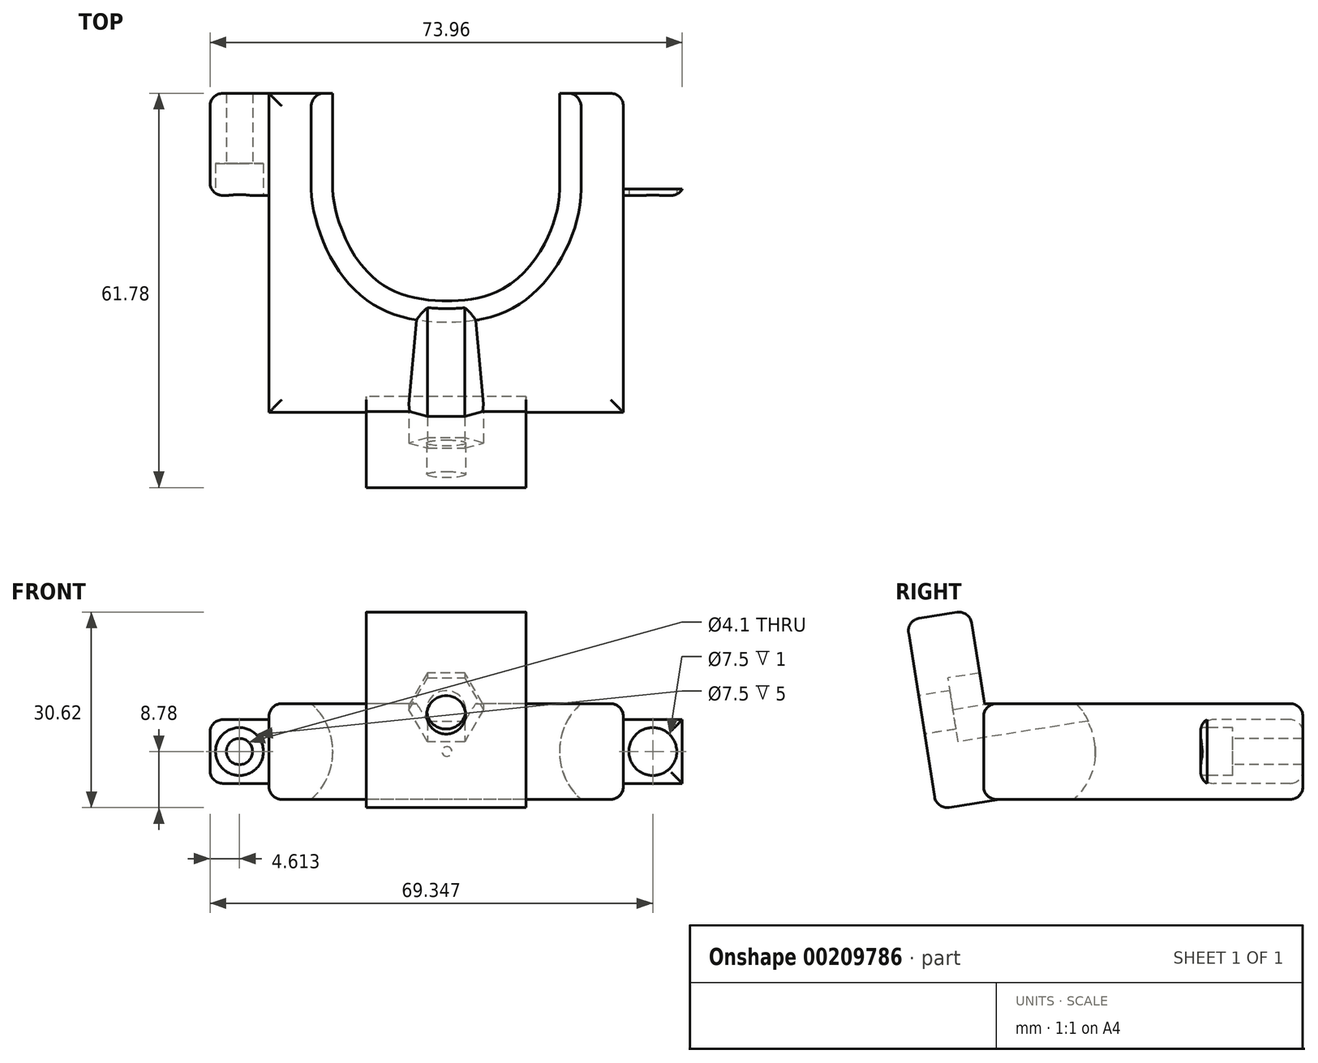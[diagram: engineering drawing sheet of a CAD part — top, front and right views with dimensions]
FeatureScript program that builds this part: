
annotation { "Feature Type Name" : "Feature", "Feature Type Description" : "" }
export const myFeature = defineFeature(function(context is Context, id is Id, definition is map)
    precondition{}
    {
        {
            var Q0;
            Q0=qCreatedBy(makeId("Front.planeOp"),FACE);
            var sketch = newSketch(context, id + "F0", { "sketchPlane" : qUnion([Q0])});
            skCircle(sketch, "E0", {"center": v(-32.37, 0) * mm, "radius": 2.05 * mm});
            skCircle(sketch, "E1.MirrorC", {"center": v(32.37, 0) * mm, "radius": 2.05 * mm});
            skLineSegment(sketch, "E2", {"start": v(-32.37, 0) * mm, "end": v(32.37, 0) * mm, "construction": true});
            skPoint(sketch, "E3", {"position": v(0, 0) * mm});
            skPoint(sketch, "E4", {"position": v(17.75, 0) * mm});
            skPoint(sketch, "E5", {"position": v(-17.75, 0) * mm});
            skLineSegment(sketch, "E6", {"start": v(27.75, -10) * mm, "end": v(27.75, 10) * mm});
            skLineSegment(sketch, "E7", {"start": v(-27.75, -10) * mm, "end": v(-27.75, 10) * mm});
            skPoint(sketch, "E8", {"position": v(-27.75, 0) * mm});
            skPoint(sketch, "E9", {"position": v(27.75, 0) * mm});
            skArc(sketch, "E10", {"start": v(-27.75, -10) * mm, "mid": v(-17.75, 0) * mm, "end": v(-27.75, 10) * mm});
            skArc(sketch, "E11", {"start": v(27.75, 10) * mm, "mid": v(17.75, 0) * mm, "end": v(27.75, -10) * mm});
            skLineSegment(sketch, "E12.bottom", {"start": v(-27.75, -5) * mm, "end": v(-36.98, -5) * mm});
            skLineSegment(sketch, "E12.top", {"start": v(-27.75, 5) * mm, "end": v(-36.98, 5) * mm});
            skLineSegment(sketch, "E12.left", {"start": v(-27.75, -5) * mm, "end": v(-27.75, 5) * mm});
            skLineSegment(sketch, "E12.right", {"start": v(-36.98, -5) * mm, "end": v(-36.98, 5) * mm});
            skLineSegment(sketch, "E13.bottom", {"start": v(27.75, 5) * mm, "end": v(36.98, 5) * mm});
            skLineSegment(sketch, "E13.top", {"start": v(27.75, -5) * mm, "end": v(36.98, -5) * mm});
            skLineSegment(sketch, "E13.left", {"start": v(27.75, 5) * mm, "end": v(27.75, -5) * mm});
            skLineSegment(sketch, "E13.right", {"start": v(36.98, 5) * mm, "end": v(36.98, -5) * mm});
            skLineSegment(sketch, "E14.bottom", {"start": v(-27.75, 7.5) * mm, "end": v(27.75, 7.5) * mm});
            skLineSegment(sketch, "E14.top", {"start": v(-27.75, -7.5) * mm, "end": v(27.75, -7.5) * mm});
            skLineSegment(sketch, "E14.left", {"start": v(-27.75, 7.5) * mm, "end": v(-27.75, -7.5) * mm});
            skLineSegment(sketch, "E14.right", {"start": v(27.75, 7.5) * mm, "end": v(27.75, -7.5) * mm});
            skCircle(sketch, "E15.cCircle", {"center": v(0, 0) * mm, "radius": 5.15 * mm, "construction": true});
            skLineSegment(sketch, "E15.0", {"start": v(-2.97, 5.15) * mm, "end": v(2.97, 5.15) * mm});
            skLineSegment(sketch, "E15.1", {"start": v(2.97, 5.15) * mm, "end": v(5.95, 0) * mm});
            skLineSegment(sketch, "E15.2", {"start": v(5.95, 0) * mm, "end": v(2.97, -5.15) * mm});
            skLineSegment(sketch, "E15.3", {"start": v(2.97, -5.15) * mm, "end": v(-2.97, -5.15) * mm});
            skLineSegment(sketch, "E15.4", {"start": v(-2.97, -5.15) * mm, "end": v(-5.95, 0) * mm});
            skLineSegment(sketch, "E15.5", {"start": v(-5.95, 0) * mm, "end": v(-2.97, 5.15) * mm});
            skPoint(sketch, "E15.0.midPoint", {"position": v(0, 5.15) * mm});
            skCircle(sketch, "E16", {"center": v(0, 0) * mm, "radius": 3.05 * mm});
            skLineSegment(sketch, "E17", {"start": v(-27.75, 0) * mm, "end": v(27.75, 0) * mm});
            skCircle(sketch, "E18", {"center": v(32.37, 0) * mm, "radius": 3.75 * mm});
            skCircle(sketch, "E19", {"center": v(-32.37, 0) * mm, "radius": 3.75 * mm});
            skSolve(sketch);
        }
        {
            var Q0;
            {var subQ2=sQuery(id+"F0.wireOp",EDGE,"E14.top");var subQ4=sQuery(id+"F0.wireOp",EDGE,"E10");var subQ5=makeQuery(id+"F0.imprint","INTERSECT",VERTEX,{"derivedFrom":[subQ4,subQ2]});Q0=makeQuery(id+"F0.imprint","IMPRINT",FACE,{"disambiguationData":[TD([[makeQuery(id+"F0.imprint","IMPRINT",EDGE,{"disambiguationData":[TD([[subQ5,-1.0]])],"derivedFrom":subQ4}),1.0]])]});}
            var Q1;
            {var subQ8=sQuery(id+"F0.wireOp",EDGE,"E15.2");Q1=makeQuery(id+"F0.imprint","IMPRINT",FACE,{"disambiguationData":[TD([[makeQuery(id+"F0.imprint","IMPRINT",EDGE,{"derivedFrom":subQ8}),1.0]])]});}
            var Q2;
            {var subQ5=sQuery(id+"F0.wireOp",EDGE,"E15.2");Q2=makeQuery(id+"F0.imprint","IMPRINT",FACE,{"disambiguationData":[TD([[makeQuery(id+"F0.imprint","IMPRINT",EDGE,{"derivedFrom":subQ5}),-1.0]])]});}
            var Q3;
            {var subQ0=sQuery(id+"F0.wireOp",EDGE,"E17");var subQ1=sQuery(id+"F0.wireOp",EDGE,"E16");var subQ2=makeQuery(id+"F0.imprint","INTERSECT",VERTEX,{"disambiguationData":[OD(0.0)],"derivedFrom":[subQ1,subQ0]});Q3=makeQuery(id+"F0.imprint","IMPRINT",FACE,{"disambiguationData":[TD([[makeQuery(id+"F0.imprint","IMPRINT",EDGE,{"disambiguationData":[TD([[subQ2,-1.0]])],"derivedFrom":subQ1}),1.0]])]});}
            var Q4;
            {var subQ2=sQuery(id+"F0.wireOp",EDGE,"E14.top");var subQ6=sQuery(id+"F0.wireOp",EDGE,"E11");var subQ7=makeQuery(id+"F0.imprint","INTERSECT",VERTEX,{"derivedFrom":[subQ6,subQ2]});Q4=makeQuery(id+"F0.imprint","IMPRINT",FACE,{"disambiguationData":[TD([[makeQuery(id+"F0.imprint","IMPRINT",EDGE,{"disambiguationData":[TD([[subQ7,1.0]])],"derivedFrom":subQ6}),1.0]])]});}
            var Q5;
            Q5=sQuery(id+"F0.wireOp",EDGE,"E17");
            revolve(context, id + "F1", {"entities" : qUnion([Q0, Q1, Q2, Q3, Q4]), "axis" : qUnion([Q5]), "revolveType" : RevolveType.ONE_DIRECTION, "angle" : 180 * degree});
        }
        {
            var Q0;
            Q0=makeQuery(id+"F0.imprint","IMPRINT",FACE,{"disambiguationData":[TD([[makeQuery(id+"F0.imprint","IMPRINT",EDGE,{"derivedFrom":sQuery(id+"F0.wireOp",EDGE,"E15.0")}),1.0]])]});
            var Q1;
            Q1=makeQuery(id+"F0.imprint","IMPRINT",FACE,{"disambiguationData":[TD([[makeQuery(id+"F0.imprint","IMPRINT",EDGE,{"derivedFrom":sQuery(id+"F0.wireOp",EDGE,"E15.0")}),-1.0]])]});
            var Q2;
            {var subQ5=sQuery(id+"F0.wireOp",EDGE,"E15.2");Q2=makeQuery(id+"F0.imprint","IMPRINT",FACE,{"disambiguationData":[TD([[makeQuery(id+"F0.imprint","IMPRINT",EDGE,{"derivedFrom":subQ5}),-1.0]])]});}
            var Q3;
            {var subQ8=sQuery(id+"F0.wireOp",EDGE,"E15.2");Q3=makeQuery(id+"F0.imprint","IMPRINT",FACE,{"disambiguationData":[TD([[makeQuery(id+"F0.imprint","IMPRINT",EDGE,{"derivedFrom":subQ8}),1.0]])]});}
            var Q4;
            {var subQ2=sQuery(id+"F0.wireOp",EDGE,"E14.top");var subQ6=sQuery(id+"F0.wireOp",EDGE,"E11");var subQ7=makeQuery(id+"F0.imprint","INTERSECT",VERTEX,{"derivedFrom":[subQ6,subQ2]});Q4=makeQuery(id+"F0.imprint","IMPRINT",FACE,{"disambiguationData":[TD([[makeQuery(id+"F0.imprint","IMPRINT",EDGE,{"disambiguationData":[TD([[subQ7,1.0]])],"derivedFrom":subQ6}),1.0]])]});}
            var Q5;
            {var subQ4=sQuery(id+"F0.wireOp",EDGE,"E11");var subQ6=sQuery(id+"F0.wireOp",EDGE,"E14.bottom");var subQ8=makeQuery(id+"F0.imprint","INTERSECT",VERTEX,{"derivedFrom":[subQ4,subQ6]});Q5=makeQuery(id+"F0.imprint","IMPRINT",FACE,{"disambiguationData":[TD([[makeQuery(id+"F0.imprint","IMPRINT",EDGE,{"disambiguationData":[TD([[subQ8,-1.0]])],"derivedFrom":subQ4}),1.0]])]});}
            var Q6;
            {var subQ4=sQuery(id+"F0.wireOp",EDGE,"E14.bottom");var subQ6=sQuery(id+"F0.wireOp",EDGE,"E10");var subQ7=makeQuery(id+"F0.imprint","INTERSECT",VERTEX,{"derivedFrom":[subQ6,subQ4]});Q6=makeQuery(id+"F0.imprint","IMPRINT",FACE,{"disambiguationData":[TD([[makeQuery(id+"F0.imprint","IMPRINT",EDGE,{"disambiguationData":[TD([[subQ7,1.0]])],"derivedFrom":subQ6}),1.0]])]});}
            var Q7;
            {var subQ2=sQuery(id+"F0.wireOp",EDGE,"E14.top");var subQ4=sQuery(id+"F0.wireOp",EDGE,"E10");var subQ5=makeQuery(id+"F0.imprint","INTERSECT",VERTEX,{"derivedFrom":[subQ4,subQ2]});Q7=makeQuery(id+"F0.imprint","IMPRINT",FACE,{"disambiguationData":[TD([[makeQuery(id+"F0.imprint","IMPRINT",EDGE,{"disambiguationData":[TD([[subQ5,-1.0]])],"derivedFrom":subQ4}),1.0]])]});}
            var Q8;
            {var subQ0=sQuery(id+"F0.wireOp",EDGE,"E17");var subQ1=sQuery(id+"F0.wireOp",EDGE,"E16");var subQ2=makeQuery(id+"F0.imprint","INTERSECT",VERTEX,{"disambiguationData":[OD(0.0)],"derivedFrom":[subQ1,subQ0]});Q8=makeQuery(id+"F0.imprint","IMPRINT",FACE,{"disambiguationData":[TD([[makeQuery(id+"F0.imprint","IMPRINT",EDGE,{"disambiguationData":[TD([[subQ2,1.0]])],"derivedFrom":subQ1}),1.0]])]});}
            var Q9;
            {var subQ0=sQuery(id+"F0.wireOp",EDGE,"E17");var subQ1=sQuery(id+"F0.wireOp",EDGE,"E16");var subQ2=makeQuery(id+"F0.imprint","INTERSECT",VERTEX,{"disambiguationData":[OD(0.0)],"derivedFrom":[subQ1,subQ0]});Q9=makeQuery(id+"F0.imprint","IMPRINT",FACE,{"disambiguationData":[TD([[makeQuery(id+"F0.imprint","IMPRINT",EDGE,{"disambiguationData":[TD([[subQ2,-1.0]])],"derivedFrom":subQ1}),1.0]])]});}
            extrude(context, id + "F2", {"entities" : qUnion([Q0, Q1, Q2, Q3, Q4, Q5, Q6, Q7, Q8, Q9]), "operationType" : NewBodyOperationType.ADD, "depth" : 10 * mm});
        }
        {
            var Q0;
            {var subQ4=sQuery(id+"F0.wireOp",EDGE,"E14.bottom");var subQ6=sQuery(id+"F0.wireOp",EDGE,"E10");var subQ7=makeQuery(id+"F0.imprint","INTERSECT",VERTEX,{"derivedFrom":[subQ6,subQ4]});Q0=makeQuery(id+"F0.imprint","IMPRINT",FACE,{"disambiguationData":[TD([[makeQuery(id+"F0.imprint","IMPRINT",EDGE,{"disambiguationData":[TD([[subQ7,1.0]])],"derivedFrom":subQ6}),1.0]])]});}
            var Q1;
            {var subQ2=sQuery(id+"F0.wireOp",EDGE,"E14.top");var subQ4=sQuery(id+"F0.wireOp",EDGE,"E10");var subQ5=makeQuery(id+"F0.imprint","INTERSECT",VERTEX,{"derivedFrom":[subQ4,subQ2]});Q1=makeQuery(id+"F0.imprint","IMPRINT",FACE,{"disambiguationData":[TD([[makeQuery(id+"F0.imprint","IMPRINT",EDGE,{"disambiguationData":[TD([[subQ5,-1.0]])],"derivedFrom":subQ4}),1.0]])]});}
            var Q2;
            {var subQ4=sQuery(id+"F0.wireOp",EDGE,"E11");var subQ6=sQuery(id+"F0.wireOp",EDGE,"E14.bottom");var subQ8=makeQuery(id+"F0.imprint","INTERSECT",VERTEX,{"derivedFrom":[subQ4,subQ6]});Q2=makeQuery(id+"F0.imprint","IMPRINT",FACE,{"disambiguationData":[TD([[makeQuery(id+"F0.imprint","IMPRINT",EDGE,{"disambiguationData":[TD([[subQ8,-1.0]])],"derivedFrom":subQ4}),1.0]])]});}
            var Q3;
            {var subQ2=sQuery(id+"F0.wireOp",EDGE,"E14.top");var subQ6=sQuery(id+"F0.wireOp",EDGE,"E11");var subQ7=makeQuery(id+"F0.imprint","INTERSECT",VERTEX,{"derivedFrom":[subQ6,subQ2]});Q3=makeQuery(id+"F0.imprint","IMPRINT",FACE,{"disambiguationData":[TD([[makeQuery(id+"F0.imprint","IMPRINT",EDGE,{"disambiguationData":[TD([[subQ7,1.0]])],"derivedFrom":subQ6}),1.0]])]});}
            extrude(context, id + "F3", {"entities" : qUnion([Q0, Q1, Q2, Q3]), "operationType" : NewBodyOperationType.ADD, "oppositeDirection" : true, "depth" : 25 * mm});
        }
        {
            var Q0;
            Q0=makeQuery(id+"F0.imprint","IMPRINT",FACE,{"disambiguationData":[TD([[makeQuery(id+"F0.imprint","IMPRINT",EDGE,{"derivedFrom":sQuery(id+"F0.wireOp",EDGE,"E0")}),-1.0]])]});
            var Q1;
            Q1=makeQuery(id+"F0.imprint","IMPRINT",FACE,{"disambiguationData":[TD([[makeQuery(id+"F0.imprint","IMPRINT",EDGE,{"derivedFrom":sQuery(id+"F0.wireOp",EDGE,"E1.MirrorC")}),1.0]])]});
            var Q2;
            {var subQ1=sQuery(id+"F0.wireOp",EDGE,"E12.bottom");Q2=makeQuery(id+"F0.imprint","IMPRINT",FACE,{"disambiguationData":[TD([[makeQuery(id+"F0.imprint","IMPRINT",EDGE,{"derivedFrom":subQ1}),-1.0]])]});}
            var Q3;
            {var subQ3=sQuery(id+"F0.wireOp",EDGE,"E13.bottom");Q3=makeQuery(id+"F0.imprint","IMPRINT",FACE,{"disambiguationData":[TD([[makeQuery(id+"F0.imprint","IMPRINT",EDGE,{"derivedFrom":subQ3}),-1.0]])]});}
            extrude(context, id + "F4", {"entities" : qUnion([Q0, Q1, Q2, Q3]), "operationType" : NewBodyOperationType.ADD, "oppositeDirection" : true, "depth" : 25 * mm, "hasSecondDirection" : true, "secondDirectionOppositeDirection" : true, "secondDirectionDepth" : 24 * mm});
        }
        {
            var Q0;
            Q0=qCreatedBy(makeId("Top.planeOp"),FACE);
            var sketch = newSketch(context, id + "F5", { "sketchPlane" : qUnion([Q0])});
            skLineSegment(sketch, "E20", {"start": v(-24.5, 7.5) * mm, "end": v(28.44, 7.5) * mm, "construction": true});
            skLineSegment(sketch, "E21", {"start": v(17.75, 0) * mm, "end": v(17.75, 25) * mm, "construction": true});
            skLineSegment(sketch, "E22", {"start": v(-17.75, 0) * mm, "end": v(-17.75, 25) * mm, "construction": true});
            skFitSpline(sketch, "E23", {"points": [v(17.75, 25) * mm, v(15, 15.7) * mm, v(8.52, 9.19) * mm, v(0, 7.5) * mm, v(-8.52, 9.19) * mm, v(-15, 15.7) * mm, v(-17.75, 25) * mm], "startDerivative": vector(0, -53.24) * mm, "endDerivative": vector(0, 41.91) * mm});
            skSolve(sketch);
        }
        {
            var Q0;
            {var subQ0=sQuery(id+"F0.wireOp",EDGE,"E14.right");Q0=makeQuery(id+"F4.boolean.opBoolean","MERGE",FACE,{"derivedFrom":[makeQuery(id+"F3.opExtrude","CAP_FACE",FACE,{"disambiguationData":[OSD([sQuery(id+"F0.wireOp",EDGE,"E11"),sQuery(id+"F0.wireOp",EDGE,"E14.bottom"),sQuery(id+"F0.wireOp",EDGE,"E14.top"),subQ0])],"isStart":false}),makeQuery(id+"F4.opExtrude","CAP_FACE",FACE,{"disambiguationData":[OSD([sQuery(id+"F0.wireOp",EDGE,"E1.MirrorC"),sQuery(id+"F0.wireOp",EDGE,"E13.bottom"),sQuery(id+"F0.wireOp",EDGE,"E13.top"),sQuery(id+"F0.wireOp",EDGE,"E13.right"),subQ0])],"isStart":false})]});}
            var sketch = newSketch(context, id + "F6", { "sketchPlane" : qUnion([Q0])});
            skLineSegment(sketch, "E24", {"start": v(-27.75, -7.5) * mm, "end": v(-27.75, 7.5) * mm});
            skArc(sketch, "E25.MirrorCS", {"start": v(-21.14, 7.5) * mm, "mid": v(-17.75, 0) * mm, "end": v(-21.14, -7.5) * mm});
            skLineSegment(sketch, "E26", {"start": v(-27.75, 7.5) * mm, "end": v(-21.14, 7.5) * mm});
            skLineSegment(sketch, "E27", {"start": v(-27.75, -7.5) * mm, "end": v(-21.14, -7.5) * mm});
            skSolve(sketch);
        }
        {
            var Q0;
            {var subQ0=sQuery(id+"F0.wireOp",EDGE,"E14.left");Q0=makeQuery(id+"F4.boolean.opBoolean","MERGE",FACE,{"derivedFrom":[makeQuery(id+"F3.opExtrude","CAP_FACE",FACE,{"disambiguationData":[OSD([sQuery(id+"F0.wireOp",EDGE,"E10"),sQuery(id+"F0.wireOp",EDGE,"E14.bottom"),sQuery(id+"F0.wireOp",EDGE,"E14.top"),subQ0])],"isStart":false}),makeQuery(id+"F4.opExtrude","CAP_FACE",FACE,{"disambiguationData":[OSD([sQuery(id+"F0.wireOp",EDGE,"E0"),sQuery(id+"F0.wireOp",EDGE,"E12.bottom"),sQuery(id+"F0.wireOp",EDGE,"E12.top"),sQuery(id+"F0.wireOp",EDGE,"E12.right"),subQ0])],"isStart":false})]});}
            var sketch = newSketch(context, id + "F7", { "sketchPlane" : qUnion([Q0])});
            skLineSegment(sketch, "E28.MirrorCS", {"start": v(27.75, -7.5) * mm, "end": v(21.14, -7.5) * mm});
            skLineSegment(sketch, "E29.MirrorCS", {"start": v(27.75, 7.5) * mm, "end": v(21.14, 7.5) * mm});
            skLineSegment(sketch, "E30.MirrorCS", {"start": v(27.75, -7.5) * mm, "end": v(27.75, 7.5) * mm});
            skArc(sketch, "E31.MirrorCS", {"start": v(21.14, 7.5) * mm, "mid": v(17.75, 0) * mm, "end": v(21.14, -7.5) * mm});
            skSolve(sketch);
        }
        {
            var Q0;
            Q0=makeQuery(id+"F6.imprint","IMPRINT",FACE,{"disambiguationData":[TD([[makeQuery(id+"F6.imprint","IMPRINT",EDGE,{"derivedFrom":sQuery(id+"F6.wireOp",EDGE,"E25.MirrorCS")}),-1.0]])]});
            var Q1;
            Q1=sQuery(id+"F5.wireOp",EDGE,"E23");
            sweep(context, id + "F8", {"operationType" : NewBodyOperationType.ADD, "profiles" : qUnion([Q0]), "path" : qUnion([Q1])});
        }
        {
            var Q0;
            Q0=makeQuery(id+"F6.imprint","IMPRINT",FACE,{"disambiguationData":[TD([[makeQuery(id+"F6.imprint","IMPRINT",EDGE,{"derivedFrom":sQuery(id+"F6.wireOp",EDGE,"E25.MirrorCS")}),-1.0]])]});
            var Q1;
            {var subQ4=sQuery(id+"F7.wireOp",EDGE,"E28.MirrorCS");Q1=makeQuery(id+"F7.imprint","IMPRINT",FACE,{"disambiguationData":[TD([[makeQuery(id+"F7.imprint","IMPRINT",EDGE,{"derivedFrom":subQ4}),-1.0]])]});}
            var Q2;
            Q2=makeQuery(id+"F7.imprint","IMPRINT",FACE,{"disambiguationData":[TD([[makeQuery(id+"F7.imprint","IMPRINT",EDGE,{"derivedFrom":makeQuery(id+"F4.opExtrude","CAP_EDGE",EDGE,{"disambiguationData":[OSD([sQuery(id+"F0.wireOp",EDGE,"E0")])],"isStart":false})}),1.0]])]});
            var Q3;
            Q3=makeQuery(id+"F6.imprint","IMPRINT",FACE,{"disambiguationData":[TD([[makeQuery(id+"F6.imprint","IMPRINT",EDGE,{"derivedFrom":makeQuery(id+"F4.opExtrude","CAP_EDGE",EDGE,{"disambiguationData":[OSD([sQuery(id+"F0.wireOp",EDGE,"E1.MirrorC")])],"isStart":false})}),-1.0]])]});
            extrude(context, id + "F9", {"entities" : qUnion([Q0, Q1, Q2, Q3]), "operationType" : NewBodyOperationType.ADD, "depth" : 15 * mm});
        }
        {
            var Q0;
            Q0=makeQuery(id+"F0.imprint","IMPRINT",FACE,{"disambiguationData":[TD([[makeQuery(id+"F0.imprint","IMPRINT",EDGE,{"derivedFrom":sQuery(id+"F0.wireOp",EDGE,"E0")}),-1.0]])]});
            var Q1;
            Q1=makeQuery(id+"F0.imprint","IMPRINT",FACE,{"disambiguationData":[TD([[makeQuery(id+"F0.imprint","IMPRINT",EDGE,{"derivedFrom":sQuery(id+"F0.wireOp",EDGE,"E1.MirrorC")}),1.0]])]});
            extrude(context, id + "F10", {"entities" : qUnion([Q0, Q1]), "operationType" : NewBodyOperationType.REMOVE, "oppositeDirection" : true, "depth" : 29 * mm});
        }
        {
            var Q0;
            {var subQ0=sQuery(id+"F6.wireOp",EDGE,"E27");var subQ1=sQuery(id+"F0.wireOp",EDGE,"E14.top");Q0=makeQuery(id+"F9.boolean.opBoolean","MERGE",FACE,{"derivedFrom":[makeQuery(id+"F8.boolean.opBoolean","MERGE",FACE,{"derivedFrom":[makeQuery(id+"F3.boolean.opBoolean","MERGE",FACE,{"derivedFrom":[makeQuery(id+"F2.opExtrude","SWEPT_FACE",FACE,{"disambiguationData":[OSD([subQ1])]}),makeQuery(id+"F3.opExtrude","SWEPT_FACE",FACE,{"disambiguationData":[OSD([subQ1]),TDD([makeQuery(id+"F0.imprint","IMPRINT",EDGE,{"disambiguationData":[TD([[makeQuery(id+"F0.imprint","INTERSECT",VERTEX,{"derivedFrom":[sQuery(id+"F0.wireOp",EDGE,"E10"),subQ1]}),1.0]])],"derivedFrom":subQ1})])]}),makeQuery(id+"F3.opExtrude","SWEPT_FACE",FACE,{"disambiguationData":[OSD([subQ1]),TDD([makeQuery(id+"F0.imprint","IMPRINT",EDGE,{"disambiguationData":[TD([[makeQuery(id+"F0.imprint","INTERSECT",VERTEX,{"derivedFrom":[sQuery(id+"F0.wireOp",EDGE,"E11"),subQ1]}),-1.0]])],"derivedFrom":subQ1})])]})]}),makeQuery(id+"F8.opSweep","SWEPT_FACE",FACE,{"disambiguationData":[OSD([sQuery(id+"F5.wireOp",EDGE,"E23"),subQ0])]})]}),makeQuery(id+"F9.opExtrude","SWEPT_FACE",FACE,{"disambiguationData":[OSD([subQ0])]}),makeQuery(id+"F9.opExtrude","SWEPT_FACE",FACE,{"disambiguationData":[OSD([sQuery(id+"F7.wireOp",EDGE,"E28.MirrorCS")])]})]});}
            var sketch = newSketch(context, id + "F11", { "sketchPlane" : qUnion([Q0])});
            skLineSegment(sketch, "E32", {"start": v(21.14, -7) * mm, "end": v(21.14, 0) * mm});
            skLineSegment(sketch, "E33", {"start": v(21.14, 0) * mm, "end": v(12.5, 0) * mm});
            skArc(sketch, "E34", {"start": v(21.14, -7) * mm, "mid": v(17.18, -3.05) * mm, "end": v(12.5, 0) * mm});
            skLineSegment(sketch, "E35", {"start": v(-12.49, 0) * mm, "end": v(-21.14, 0) * mm});
            skLineSegment(sketch, "E36", {"start": v(-21.14, 0) * mm, "end": v(-21.14, -6.91) * mm});
            skArc(sketch, "E37", {"start": v(-12.49, 0) * mm, "mid": v(-17.17, -3) * mm, "end": v(-21.14, -6.91) * mm});
            skSolve(sketch);
        }
        {
            var Q0;
            Q0 = qSketchRegion(id + "F11", true);
            var Q1;
            {var subQ0=sQuery(id+"F6.wireOp",EDGE,"E26");var subQ1=sQuery(id+"F0.wireOp",EDGE,"E14.bottom");Q1=makeQuery(id+"F9.boolean.opBoolean","MERGE",FACE,{"derivedFrom":[makeQuery(id+"F8.boolean.opBoolean","MERGE",FACE,{"derivedFrom":[makeQuery(id+"F3.boolean.opBoolean","MERGE",FACE,{"derivedFrom":[makeQuery(id+"F2.opExtrude","SWEPT_FACE",FACE,{"disambiguationData":[OSD([subQ1])]}),makeQuery(id+"F3.opExtrude","SWEPT_FACE",FACE,{"disambiguationData":[OSD([subQ1]),TDD([makeQuery(id+"F0.imprint","IMPRINT",EDGE,{"disambiguationData":[TD([[makeQuery(id+"F0.imprint","INTERSECT",VERTEX,{"derivedFrom":[sQuery(id+"F0.wireOp",EDGE,"E10"),subQ1]}),1.0]])],"derivedFrom":subQ1})])]}),makeQuery(id+"F3.opExtrude","SWEPT_FACE",FACE,{"disambiguationData":[OSD([subQ1]),TDD([makeQuery(id+"F0.imprint","IMPRINT",EDGE,{"disambiguationData":[TD([[makeQuery(id+"F0.imprint","INTERSECT",VERTEX,{"derivedFrom":[sQuery(id+"F0.wireOp",EDGE,"E11"),subQ1]}),-1.0]])],"derivedFrom":subQ1})])]})]}),makeQuery(id+"F8.opSweep","SWEPT_FACE",FACE,{"disambiguationData":[OSD([sQuery(id+"F5.wireOp",EDGE,"E23"),subQ0])]})]}),makeQuery(id+"F9.opExtrude","SWEPT_FACE",FACE,{"disambiguationData":[OSD([subQ0])]}),makeQuery(id+"F9.opExtrude","SWEPT_FACE",FACE,{"disambiguationData":[OSD([sQuery(id+"F7.wireOp",EDGE,"E29.MirrorCS")])]})]});}
            extrude(context, id + "F12", {"entities" : qUnion([Q0]), "operationType" : NewBodyOperationType.ADD, "endBound" : BoundingType.UP_TO_SURFACE, "oppositeDirection" : true, "endBoundEntityFace" : qUnion([Q1]), "depth" : 15 * mm});
        }
        {
            var Q0;
            Q0=qCreatedBy(makeId("Right.planeOp"),FACE);
            var sketch = newSketch(context, id + "F13", { "sketchPlane" : qUnion([Q0])});
            skLineSegment(sketch, "E38", {"start": v(0, 0) * mm, "end": v(-10, 0) * mm, "construction": true});
            skLineSegment(sketch, "E39", {"start": v(-10, 0) * mm, "end": v(-10, -41.96) * mm, "construction": true});
            skLineSegment(sketch, "E40", {"start": v(-10, 0) * mm, "end": v(-10, 41.96) * mm, "construction": true});
            skLineSegment(sketch, "E41", {"start": v(-11.88, 20.16) * mm, "end": v(-7.5, -7.5) * mm});
            skLineSegment(sketch, "E42", {"start": v(-7.5, -7.5) * mm, "end": v(-15.4, -8.75) * mm});
            skLineSegment(sketch, "E43", {"start": v(-17.69, -7.09) * mm, "end": v(-21.76, 18.6) * mm});
            skLineSegment(sketch, "E44", {"start": v(-20.1, 20.88) * mm, "end": v(-14.17, 21.82) * mm});
            skPoint(sketch, "E45", {"position": v(-10, -5) * mm});
            skLineSegment(sketch, "E46", {"start": v(0, 0) * mm, "end": v(0, -7.5) * mm, "construction": true});
            skLineSegment(sketch, "E47", {"start": v(0, -7.5) * mm, "end": v(-7.5, -7.5) * mm, "construction": true});
            skPoint(sketch, "E48", {"position": v(-7.5, -7.5) * mm});
            skPoint(sketch, "E49", {"position": v(-9.85, 7.32) * mm});
            skPoint(sketch, "E50", {"position": v(-19.72, 5.75) * mm});
            skLineSegment(sketch, "E51", {"start": v(-19.72, 5.75) * mm, "end": v(-9.85, 7.32) * mm});
            skPoint(sketch, "E52.visualSharp", {"position": v(-22.07, 20.57) * mm});
            skArc(sketch, "E52.filletArc", {"start": v(-20.1, 20.88) * mm, "mid": v(-21.4, 20.08) * mm, "end": v(-21.76, 18.6) * mm});
            skPoint(sketch, "E53.visualSharp", {"position": v(-17.38, -9.06) * mm});
            skArc(sketch, "E53.filletArc", {"start": v(-17.69, -7.09) * mm, "mid": v(-16.89, -8.4) * mm, "end": v(-15.4, -8.75) * mm});
            skPoint(sketch, "E54.visualSharp", {"position": v(-12.2, 22.13) * mm});
            skArc(sketch, "E54.filletArc", {"start": v(-11.88, 20.16) * mm, "mid": v(-12.68, 21.46) * mm, "end": v(-14.17, 21.82) * mm});
            skSolve(sketch);
        }
        {
            var Q0;
            Q0=makeQuery(id+"F13.imprint","IMPRINT",FACE,{"disambiguationData":[TD([[makeQuery(id+"F13.imprint","IMPRINT",EDGE,{"derivedFrom":sQuery(id+"F13.wireOp",EDGE,"E44")}),-1.0]])]});
            var Q1;
            {var subQ1=sQuery(id+"F13.wireOp",EDGE,"E42");Q1=makeQuery(id+"F13.imprint","IMPRINT",FACE,{"disambiguationData":[TD([[makeQuery(id+"F13.imprint","IMPRINT",EDGE,{"derivedFrom":subQ1}),-1.0]])]});}
            extrude(context, id + "F14", {"entities" : qUnion([Q0, Q1]), "operationType" : NewBodyOperationType.ADD, "depth" : 25 * mm, "symmetric" : true});
        }
        {
            var Q0;
            Q0=makeQuery(id+"F14.opExtrude","SWEPT_FACE",FACE,{"disambiguationData":[OSD([sQuery(id+"F13.wireOp",EDGE,"E43")])]});
            var sketch = newSketch(context, id + "F15", { "sketchPlane" : qUnion([Q0])});
            skPoint(sketch, "E55", {"position": v(0, 8.77) * mm});
            skCircle(sketch, "E56.cCircle", {"center": v(0, 8.77) * mm, "radius": 5.05 * mm, "construction": true});
            skLineSegment(sketch, "E56.0", {"start": v(-2.92, 13.82) * mm, "end": v(2.92, 13.82) * mm});
            skLineSegment(sketch, "E56.1", {"start": v(2.92, 13.82) * mm, "end": v(5.83, 8.77) * mm});
            skLineSegment(sketch, "E56.2", {"start": v(5.83, 8.77) * mm, "end": v(2.92, 3.72) * mm});
            skLineSegment(sketch, "E56.3", {"start": v(2.92, 3.72) * mm, "end": v(-2.92, 3.72) * mm});
            skLineSegment(sketch, "E56.4", {"start": v(-2.92, 3.72) * mm, "end": v(-5.83, 8.77) * mm});
            skLineSegment(sketch, "E56.5", {"start": v(-5.83, 8.77) * mm, "end": v(-2.92, 13.82) * mm});
            skPoint(sketch, "E56.0.midPoint", {"position": v(0, 13.82) * mm});
            skCircle(sketch, "E57", {"center": v(0, 8.77) * mm, "radius": 3.05 * mm});
            skSolve(sketch);
        }
        {
            var Q0;
            Q0=makeQuery(id+"F15.imprint","IMPRINT",FACE,{"disambiguationData":[TD([[makeQuery(id+"F15.imprint","IMPRINT",EDGE,{"derivedFrom":sQuery(id+"F15.wireOp",EDGE,"E57")}),1.0]])]});
            extrude(context, id + "F16", {"entities" : qUnion([Q0]), "operationType" : NewBodyOperationType.REMOVE, "oppositeDirection" : true, "depth" : 25 * mm});
        }
        {
            var Q0;
            Q0=makeQuery(id+"F15.imprint","IMPRINT",FACE,{"disambiguationData":[TD([[makeQuery(id+"F15.imprint","IMPRINT",EDGE,{"derivedFrom":sQuery(id+"F15.wireOp",EDGE,"E56.0")}),-1.0]])]});
            extrude(context, id + "F17", {"entities" : qUnion([Q0]), "operationType" : NewBodyOperationType.REMOVE, "oppositeDirection" : true, "depth" : 30 * mm, "hasSecondDirection" : true, "secondDirectionOppositeDirection" : true, "secondDirectionDepth" : 5 * mm});
        }
        {
            var Q0;
            {var subQ0=sQuery(id+"F0.wireOp",EDGE,"E12.right");var subQ1=sQuery(id+"F0.wireOp",EDGE,"E12.bottom");Q0=makeQuery(id+"F9.boolean.opBoolean","MERGE",EDGE,{"derivedFrom":[makeQuery(id+"F4.boolean.opBoolean","MERGE",EDGE,{"derivedFrom":[makeQuery(id+"F2.opExtrude","SWEPT_EDGE",EDGE,{"disambiguationData":[OSD([subQ1,subQ0])]}),makeQuery(id+"F4.opExtrude","SWEPT_EDGE",EDGE,{"disambiguationData":[OSD([subQ1,subQ0])]})]}),makeQuery(id+"F9.opExtrude","SWEPT_EDGE",EDGE,{"disambiguationData":[OSD([subQ1,subQ0])]})]});}
            var Q1;
            {var subQ0=sQuery(id+"F0.wireOp",EDGE,"E12.right");var subQ1=sQuery(id+"F0.wireOp",EDGE,"E12.top");Q1=makeQuery(id+"F9.boolean.opBoolean","MERGE",EDGE,{"derivedFrom":[makeQuery(id+"F4.boolean.opBoolean","MERGE",EDGE,{"derivedFrom":[makeQuery(id+"F2.opExtrude","SWEPT_EDGE",EDGE,{"disambiguationData":[OSD([subQ1,subQ0])]}),makeQuery(id+"F4.opExtrude","SWEPT_EDGE",EDGE,{"disambiguationData":[OSD([subQ1,subQ0])]})]}),makeQuery(id+"F9.opExtrude","SWEPT_EDGE",EDGE,{"disambiguationData":[OSD([subQ1,subQ0])]})]});}
            var Q2;
            Q2=makeQuery(id+"F9.opExtrude","CAP_EDGE",EDGE,{"disambiguationData":[OSD([sQuery(id+"F0.wireOp",EDGE,"E12.right")])],"isStart":false});
            var Q3;
            Q3=makeQuery(id+"F9.opExtrude","CAP_EDGE",EDGE,{"disambiguationData":[OSD([sQuery(id+"F0.wireOp",EDGE,"E12.top")])],"isStart":false});
            var Q4;
            Q4=makeQuery(id+"F9.opExtrude","CAP_EDGE",EDGE,{"disambiguationData":[OSD([sQuery(id+"F0.wireOp",EDGE,"E12.bottom")])],"isStart":false});
            var Q5;
            {var subQ0=sQuery(id+"F7.wireOp",EDGE,"E30.MirrorCS");Q5=makeQuery(id+"F9.opExtrude","CAP_EDGE",EDGE,{"disambiguationData":[OSD([subQ0]),TDD([makeQuery(id+"F7.imprint","IMPRINT",EDGE,{"disambiguationData":[TD([[makeQuery(id+"F7.imprint","INTERSECT",VERTEX,{"derivedFrom":[sQuery(id+"F7.wireOp",EDGE,"E28.MirrorCS"),subQ0]}),1.0],[makeQuery(id+"F7.imprint","INTERSECT",VERTEX,{"derivedFrom":[makeQuery(id+"F4.opExtrude","CAP_EDGE",EDGE,{"disambiguationData":[OSD([sQuery(id+"F0.wireOp",EDGE,"E12.bottom")])],"isStart":false}),subQ0]}),-1.0]])],"derivedFrom":subQ0})])],"isStart":false});}
            var Q6;
            {var subQ0=sQuery(id+"F0.wireOp",EDGE,"E14.left");var subQ1=sQuery(id+"F0.wireOp",EDGE,"E14.top");var subQ2=sQuery(id+"F0.wireOp",EDGE,"E7");Q6=makeQuery(id+"F9.boolean.opBoolean","MERGE",EDGE,{"derivedFrom":[makeQuery(id+"F3.boolean.opBoolean","MERGE",EDGE,{"derivedFrom":[makeQuery(id+"F2.opExtrude","SWEPT_EDGE",EDGE,{"disambiguationData":[OSD([subQ2,subQ1,subQ0])]}),makeQuery(id+"F3.opExtrude","SWEPT_EDGE",EDGE,{"disambiguationData":[OSD([subQ2,subQ1,subQ0])]})]}),makeQuery(id+"F9.opExtrude","SWEPT_EDGE",EDGE,{"disambiguationData":[OSD([sQuery(id+"F7.wireOp",EDGE,"E28.MirrorCS"),sQuery(id+"F7.wireOp",EDGE,"E30.MirrorCS")])]})]});}
            var Q7;
            Q7=makeQuery(id+"F9.opExtrude","CAP_EDGE",EDGE,{"disambiguationData":[OSD([sQuery(id+"F7.wireOp",EDGE,"E28.MirrorCS")])],"isStart":false});
            var Q8;
            {var subQ0=sQuery(id+"F7.wireOp",EDGE,"E30.MirrorCS");Q8=makeQuery(id+"F9.opExtrude","CAP_EDGE",EDGE,{"disambiguationData":[OSD([subQ0]),TDD([makeQuery(id+"F7.imprint","IMPRINT",EDGE,{"disambiguationData":[TD([[makeQuery(id+"F7.imprint","INTERSECT",VERTEX,{"derivedFrom":[sQuery(id+"F7.wireOp",EDGE,"E29.MirrorCS"),subQ0]}),-1.0],[makeQuery(id+"F7.imprint","INTERSECT",VERTEX,{"derivedFrom":[makeQuery(id+"F4.opExtrude","CAP_EDGE",EDGE,{"disambiguationData":[OSD([sQuery(id+"F0.wireOp",EDGE,"E12.top")])],"isStart":false}),subQ0]}),1.0]])],"derivedFrom":subQ0})])],"isStart":false});}
            var Q9;
            Q9=makeQuery(id+"F9.opExtrude","CAP_EDGE",EDGE,{"disambiguationData":[OSD([sQuery(id+"F7.wireOp",EDGE,"E29.MirrorCS")])],"isStart":false});
            var Q10;
            Q10=makeQuery(id+"F9.opExtrude","CAP_EDGE",EDGE,{"disambiguationData":[OSD([sQuery(id+"F6.wireOp",EDGE,"E27")])],"isStart":false});
            var Q11;
            {var subQ0=sQuery(id+"F6.wireOp",EDGE,"E24");Q11=makeQuery(id+"F9.opExtrude","CAP_EDGE",EDGE,{"disambiguationData":[OSD([subQ0]),TDD([makeQuery(id+"F6.imprint","IMPRINT",EDGE,{"disambiguationData":[TD([[makeQuery(id+"F6.imprint","INTERSECT",VERTEX,{"derivedFrom":[subQ0,sQuery(id+"F6.wireOp",EDGE,"E27")]}),1.0],[makeQuery(id+"F6.imprint","INTERSECT",VERTEX,{"derivedFrom":[makeQuery(id+"F4.opExtrude","CAP_EDGE",EDGE,{"disambiguationData":[OSD([sQuery(id+"F0.wireOp",EDGE,"E13.top")])],"isStart":false}),subQ0]}),-1.0]])],"derivedFrom":subQ0})])],"isStart":false});}
            var Q12;
            Q12=makeQuery(id+"F9.opExtrude","CAP_EDGE",EDGE,{"disambiguationData":[OSD([sQuery(id+"F0.wireOp",EDGE,"E13.top")])],"isStart":false});
            var Q13;
            Q13=makeQuery(id+"F9.opExtrude","CAP_EDGE",EDGE,{"disambiguationData":[OSD([sQuery(id+"F0.wireOp",EDGE,"E13.right")])],"isStart":false});
            var Q14;
            Q14=makeQuery(id+"F9.opExtrude","CAP_EDGE",EDGE,{"disambiguationData":[OSD([sQuery(id+"F0.wireOp",EDGE,"E13.bottom")])],"isStart":false});
            var Q15;
            {var subQ0=sQuery(id+"F6.wireOp",EDGE,"E24");Q15=makeQuery(id+"F9.opExtrude","CAP_EDGE",EDGE,{"disambiguationData":[OSD([subQ0]),TDD([makeQuery(id+"F6.imprint","IMPRINT",EDGE,{"disambiguationData":[TD([[makeQuery(id+"F6.imprint","INTERSECT",VERTEX,{"derivedFrom":[subQ0,sQuery(id+"F6.wireOp",EDGE,"E26")]}),-1.0],[makeQuery(id+"F6.imprint","INTERSECT",VERTEX,{"derivedFrom":[makeQuery(id+"F4.opExtrude","CAP_EDGE",EDGE,{"disambiguationData":[OSD([sQuery(id+"F0.wireOp",EDGE,"E13.bottom")])],"isStart":false}),subQ0]}),1.0]])],"derivedFrom":subQ0})])],"isStart":false});}
            var Q16;
            Q16=makeQuery(id+"F9.opExtrude","CAP_EDGE",EDGE,{"disambiguationData":[OSD([sQuery(id+"F6.wireOp",EDGE,"E26")])],"isStart":false});
            var Q17;
            {var subQ0=sQuery(id+"F0.wireOp",EDGE,"E14.right");var subQ1=sQuery(id+"F0.wireOp",EDGE,"E14.top");var subQ2=sQuery(id+"F0.wireOp",EDGE,"E6");Q17=makeQuery(id+"F9.boolean.opBoolean","MERGE",EDGE,{"derivedFrom":[makeQuery(id+"F3.boolean.opBoolean","MERGE",EDGE,{"derivedFrom":[makeQuery(id+"F2.opExtrude","SWEPT_EDGE",EDGE,{"disambiguationData":[OSD([subQ2,subQ1,subQ0])]}),makeQuery(id+"F3.opExtrude","SWEPT_EDGE",EDGE,{"disambiguationData":[OSD([subQ2,subQ1,subQ0])]})]}),makeQuery(id+"F9.opExtrude","SWEPT_EDGE",EDGE,{"disambiguationData":[OSD([sQuery(id+"F6.wireOp",EDGE,"E24"),sQuery(id+"F6.wireOp",EDGE,"E27")])]})]});}
            var Q18;
            {var subQ0=sQuery(id+"F0.wireOp",EDGE,"E13.right");var subQ1=sQuery(id+"F0.wireOp",EDGE,"E13.top");Q18=makeQuery(id+"F9.boolean.opBoolean","MERGE",EDGE,{"derivedFrom":[makeQuery(id+"F4.boolean.opBoolean","MERGE",EDGE,{"derivedFrom":[makeQuery(id+"F2.opExtrude","SWEPT_EDGE",EDGE,{"disambiguationData":[OSD([subQ1,subQ0])]}),makeQuery(id+"F4.opExtrude","SWEPT_EDGE",EDGE,{"disambiguationData":[OSD([subQ1,subQ0])]})]}),makeQuery(id+"F9.opExtrude","SWEPT_EDGE",EDGE,{"disambiguationData":[OSD([subQ1,subQ0])]})]});}
            var Q19;
            {var subQ0=sQuery(id+"F0.wireOp",EDGE,"E13.right");var subQ1=sQuery(id+"F0.wireOp",EDGE,"E13.bottom");Q19=makeQuery(id+"F9.boolean.opBoolean","MERGE",EDGE,{"derivedFrom":[makeQuery(id+"F4.boolean.opBoolean","MERGE",EDGE,{"derivedFrom":[makeQuery(id+"F2.opExtrude","SWEPT_EDGE",EDGE,{"disambiguationData":[OSD([subQ1,subQ0])]}),makeQuery(id+"F4.opExtrude","SWEPT_EDGE",EDGE,{"disambiguationData":[OSD([subQ1,subQ0])]})]}),makeQuery(id+"F9.opExtrude","SWEPT_EDGE",EDGE,{"disambiguationData":[OSD([subQ1,subQ0])]})]});}
            var Q20;
            {var subQ0=sQuery(id+"F0.wireOp",EDGE,"E14.right");var subQ1=sQuery(id+"F0.wireOp",EDGE,"E14.bottom");var subQ2=sQuery(id+"F0.wireOp",EDGE,"E6");Q20=makeQuery(id+"F9.boolean.opBoolean","MERGE",EDGE,{"derivedFrom":[makeQuery(id+"F3.boolean.opBoolean","MERGE",EDGE,{"derivedFrom":[makeQuery(id+"F2.opExtrude","SWEPT_EDGE",EDGE,{"disambiguationData":[OSD([subQ2,subQ1,subQ0])]}),makeQuery(id+"F3.opExtrude","SWEPT_EDGE",EDGE,{"disambiguationData":[OSD([subQ2,subQ1,subQ0])]})]}),makeQuery(id+"F9.opExtrude","SWEPT_EDGE",EDGE,{"disambiguationData":[OSD([sQuery(id+"F6.wireOp",EDGE,"E24"),sQuery(id+"F6.wireOp",EDGE,"E26")])]})]});}
            var Q21;
            {var subQ0=sQuery(id+"F0.wireOp",EDGE,"E14.left");var subQ1=sQuery(id+"F0.wireOp",EDGE,"E14.bottom");var subQ2=sQuery(id+"F0.wireOp",EDGE,"E7");Q21=makeQuery(id+"F9.boolean.opBoolean","MERGE",EDGE,{"derivedFrom":[makeQuery(id+"F3.boolean.opBoolean","MERGE",EDGE,{"derivedFrom":[makeQuery(id+"F2.opExtrude","SWEPT_EDGE",EDGE,{"disambiguationData":[OSD([subQ2,subQ1,subQ0])]}),makeQuery(id+"F3.opExtrude","SWEPT_EDGE",EDGE,{"disambiguationData":[OSD([subQ2,subQ1,subQ0])]})]}),makeQuery(id+"F9.opExtrude","SWEPT_EDGE",EDGE,{"disambiguationData":[OSD([sQuery(id+"F7.wireOp",EDGE,"E29.MirrorCS"),sQuery(id+"F7.wireOp",EDGE,"E30.MirrorCS")])]})]});}
            var Q22;
            Q22=makeQuery(id+"F2.opExtrude","CAP_EDGE",EDGE,{"disambiguationData":[OSD([sQuery(id+"F0.wireOp",EDGE,"E12.top")])],"isStart":false});
            var Q23;
            Q23=makeQuery(id+"F2.opExtrude","CAP_EDGE",EDGE,{"disambiguationData":[OSD([sQuery(id+"F0.wireOp",EDGE,"E12.right")])],"isStart":false});
            var Q24;
            Q24=makeQuery(id+"F2.opExtrude","CAP_EDGE",EDGE,{"disambiguationData":[OSD([sQuery(id+"F0.wireOp",EDGE,"E12.bottom")])],"isStart":false});
            var Q25;
            Q25=makeQuery(id+"F2.opExtrude","CAP_EDGE",EDGE,{"disambiguationData":[OSD([sQuery(id+"F0.wireOp",EDGE,"E14.top")])],"isStart":false});
            var Q26;
            Q26=makeQuery(id+"F2.opExtrude","CAP_EDGE",EDGE,{"disambiguationData":[OSD([sQuery(id+"F0.wireOp",EDGE,"E13.top")])],"isStart":false});
            var Q27;
            Q27=makeQuery(id+"F2.opExtrude","CAP_EDGE",EDGE,{"disambiguationData":[OSD([sQuery(id+"F0.wireOp",EDGE,"E13.right")])],"isStart":false});
            var Q28;
            Q28=makeQuery(id+"F2.opExtrude","CAP_EDGE",EDGE,{"disambiguationData":[OSD([sQuery(id+"F0.wireOp",EDGE,"E13.bottom")])],"isStart":false});
            var Q29;
            Q29=makeQuery(id+"F2.opExtrude","CAP_EDGE",EDGE,{"disambiguationData":[OSD([sQuery(id+"F0.wireOp",EDGE,"E14.bottom")])],"isStart":false});
            var Q30;
            Q30=makeQuery(id+"F4.opExtrude","CAP_EDGE",EDGE,{"disambiguationData":[OSD([sQuery(id+"F0.wireOp",EDGE,"E12.bottom")])],"isStart":true});
            var Q31;
            Q31=makeQuery(id+"F4.opExtrude","CAP_EDGE",EDGE,{"disambiguationData":[OSD([sQuery(id+"F0.wireOp",EDGE,"E12.top")])],"isStart":true});
            var Q32;
            Q32=makeQuery(id+"F4.opExtrude","CAP_EDGE",EDGE,{"disambiguationData":[OSD([sQuery(id+"F0.wireOp",EDGE,"E12.right")])],"isStart":true});
            var Q33;
            Q33=makeQuery(id+"F2.opExtrude","CAP_EDGE",EDGE,{"disambiguationData":[OSD([sQuery(id+"F0.wireOp",EDGE,"E14.left")])],"isStart":false});
            var Q34;
            Q34=makeQuery(id+"F2.opExtrude","CAP_EDGE",EDGE,{"disambiguationData":[OSD([sQuery(id+"F0.wireOp",EDGE,"E14.right")])],"isStart":false});
            var Q35;
            Q35=makeQuery(id+"F4.opExtrude","CAP_EDGE",EDGE,{"disambiguationData":[OSD([sQuery(id+"F0.wireOp",EDGE,"E13.right")])],"isStart":true});
            var Q36;
            Q36=makeQuery(id+"F4.opExtrude","CAP_EDGE",EDGE,{"disambiguationData":[OSD([sQuery(id+"F0.wireOp",EDGE,"E13.top")])],"isStart":true});
            var Q37;
            Q37=makeQuery(id+"F4.opExtrude","CAP_EDGE",EDGE,{"disambiguationData":[OSD([sQuery(id+"F0.wireOp",EDGE,"E13.bottom")])],"isStart":true});
            fillet(context, id + "F18", {"entities" : qUnion([Q0, Q1, Q2, Q3, Q4, Q5, Q6, Q7, Q8, Q9, Q10, Q11, Q12, Q13, Q14, Q15, Q16, Q17, Q18, Q19, Q20, Q21, Q22, Q23, Q24, Q25, Q26, Q27, Q28, Q29, Q30, Q31, Q32, Q33, Q34, Q35, Q36, Q37]), "radius" : 2 * mm, "tangentPropagation" : true, "allowEdgeOverflow" : false});
        }
    });
